# Revit family: Hager-Vega-IP40-syst-NoHosted-BE-en
name_source: partatom
category: Electrical Equipment
units: mm (PartAtom-declared; Revit-internal decimal feet)

## family parameters
Always vertical = Yes
Cut with Voids When Loaded = No
Panel Configuration = Two Columns, Circuits Across
Part Type = Panelboard
Room Calculation Point = No
Round Connector Dimension = Use Diameter
Shared = No
Work Plane-Based = Yes

## types (14) — shared parameters
Default Elevation = 1219 mm
EF000003 - Mounting method = EV000384 - Surface mounted (plaster)
EF000007 - Colour = EV000202 - White
EF000008 - Width = 400 mm  [stored 1.31234 ft]
EF000049 - Depth = 146 mm  [stored 0.479003 ft]
EF000116 - RAL-number = 9010
EF000339 - Type of cover = EV004216 - Door
EF001062 - EMC-version = No
EF001088 - Extension possible = Yes
EF001134 - DIN-rail = Yes
EF001596 - Material housing = EV000139 - Plastic
EF002950 - Width in number of modular spacings = 18
EF004462 - Type of closure = EV000154 - Other
EF006306 - With lock = No
EF015777 - Neutral terminal block = No
EF015941 - Signal passing door = Yes
HG000001 - Number of columns = 1
HG000002 - With door or cover = Yes
HG000003 - Range = Vega
HG000005 - Thickness = 3 mm  [stored 0.00984252 ft]
HG000006 - Flush mounted = No
HG000009 - Double swing door = No
HG000010 - Asymmetric doors = No
HG000017 - Distance between poles = 18 mm  [stored 0.0590551 ft]
Manufacturer = Hager
Type Comments = Vega
zero-valued in all types: EF000218 - Built-in depth, EF000332 - Built-in height, EF000846 - Built-in width, HG000007 - Number of empty columns

## per-type parameters (varying)
| type | EF000040 - Height | EF000118 - With mounting plate | EF000266 - Number of rows | EF001131 - Internal depth | EF005474 - Degree of protection (IP) | EF006244 - Transparent cover/door | EF009212 - Cover model | EF015776 - Earthing terminal block | HG000004 - Manufacturer reference | HG000008 - Number of empty rows | HG000011 - Empty rows from bottom | Model |
| Surface mounted IP40 W400 H325 D146 18 Modular spacings - VB118B | 325 mm  [stored 1.06627 ft] | No | 1 | 120 mm  [stored 0.393701 ft] | EV006415 - IP40 | No | EV000116 - Closed | Yes | VB118B | 0 | No | VB118B |
| Surface mounted IP40 W400 H325 D146 18 Modular spacings - VB118R | 325 mm  [stored 1.06627 ft] | No | 1 | 120 mm  [stored 0.393701 ft] | EV006415 - IP40 | Yes | EV000116 - Closed | Yes | VB118R | 0 | No | VB118R |
| Surface mounted IP40 W400 H475 D146 18 Modular spacings - VB218B | 475 mm  [stored 1.5584 ft] | No | 2 | 120 mm  [stored 0.393701 ft] | EV006415 - IP40 | No | EV000116 - Closed | Yes | VB218B | 0 | No | VB218B |
| Surface mounted IP40 W400 H475 D146 18 Modular spacings - VB218R | 475 mm  [stored 1.5584 ft] | No | 2 | 120 mm  [stored 0.393701 ft] | EV006415 - IP40 | Yes | EV000116 - Closed | Yes | VB218R | 0 | No | VB218R |
| Surface mounted IP40 W400 H625 D146 18 Modular spacings - VB318B | 625 mm  [stored 2.05052 ft] | No | 3 | 120 mm  [stored 0.393701 ft] | EV006415 - IP40 | No | EV000116 - Closed | Yes | VB318B | 0 | No | VB318B |
| Surface mounted IP40 W400 H625 D146 18 Modular spacings - VB318R | 625 mm  [stored 2.05052 ft] | No | 3 | 120 mm  [stored 0.393701 ft] | EV006415 - IP40 | Yes | EV000116 - Closed | Yes | VB318R | 0 | No | VB318R |
| Surface mounted IP40 W400 H775 D146 18 Modular spacings - VB418B | 775 mm  [stored 2.54265 ft] | No | 4 | 120 mm  [stored 0.393701 ft] | EV006415 - IP40 | No | EV000116 - Closed | Yes | VB418B | 0 | No | VB418B |
| Surface mounted IP40 W400 H775 D146 18 Modular spacings - VB418R | 775 mm  [stored 2.54265 ft] | No | 4 | 120 mm  [stored 0.393701 ft] | EV006415 - IP40 | Yes | EV000116 - Closed | Yes | VB418R | 0 | No | VB418R |
| Surface mounted ther W400 H625 D146 18 Modular spacings - VB318MMP | 625 mm  [stored 2.05052 ft] | Yes | 1 | 140 mm  [stored 0.459318 ft] | EV000154 - Other | No | EV009916 - With notch | No | VB318MMP | 2 | Yes | VB318MMP |
| Surface mounted ther W400 H625 D146 18 Modular spacings - VB318MMT | 625 mm  [stored 2.05052 ft] | Yes | 1 | 140 mm  [stored 0.459318 ft] | EV000154 - Other | Yes | EV009916 - With notch | No | VB318MMT | 2 | Yes | VB318MMT |
| Surface mounted ther W400 H775 D146 18 Modular spacings - VB418MMP | 775 mm  [stored 2.54265 ft] | Yes | 1 | 140 mm  [stored 0.459318 ft] | EV000154 - Other | No | EV009916 - With notch | No | VB418MMP | 3 | Yes | VB418MMP |
| Surface mounted ther W400 H775 D146 18 Modular spacings - VB418MMT | 775 mm  [stored 2.54265 ft] | Yes | 1 | 140 mm  [stored 0.459318 ft] | EV000154 - Other | Yes | EV009916 - With notch | No | VB418MMT | 3 | Yes | VB418MMT |
| Surface mounted ther W400 H775 D146 18 Modular spacings - VB418MTP | 775 mm  [stored 2.54265 ft] | Yes | 2 | 140 mm  [stored 0.459318 ft] | EV000154 - Other | Yes | EV009916 - With notch | No | VB418MTP | 2 | Yes | VB418MTP |
| Surface mounted ther W400 H775 D146 18 Modular spacings - VB418MTT | 775 mm  [stored 2.54265 ft] | Yes | 2 | 140 mm  [stored 0.459318 ft] | EV000154 - Other | Yes | EV009916 - With notch | No | VB418MTT | 2 | Yes | VB418MTT |

note: [stored X ft] marks values corroborated as IEEE doubles in the binary element streams (Revit-internal decimal feet)

## geometry (parser evidence)
native form markers: Sweep x14
no freeform markers — native parametric forms only
